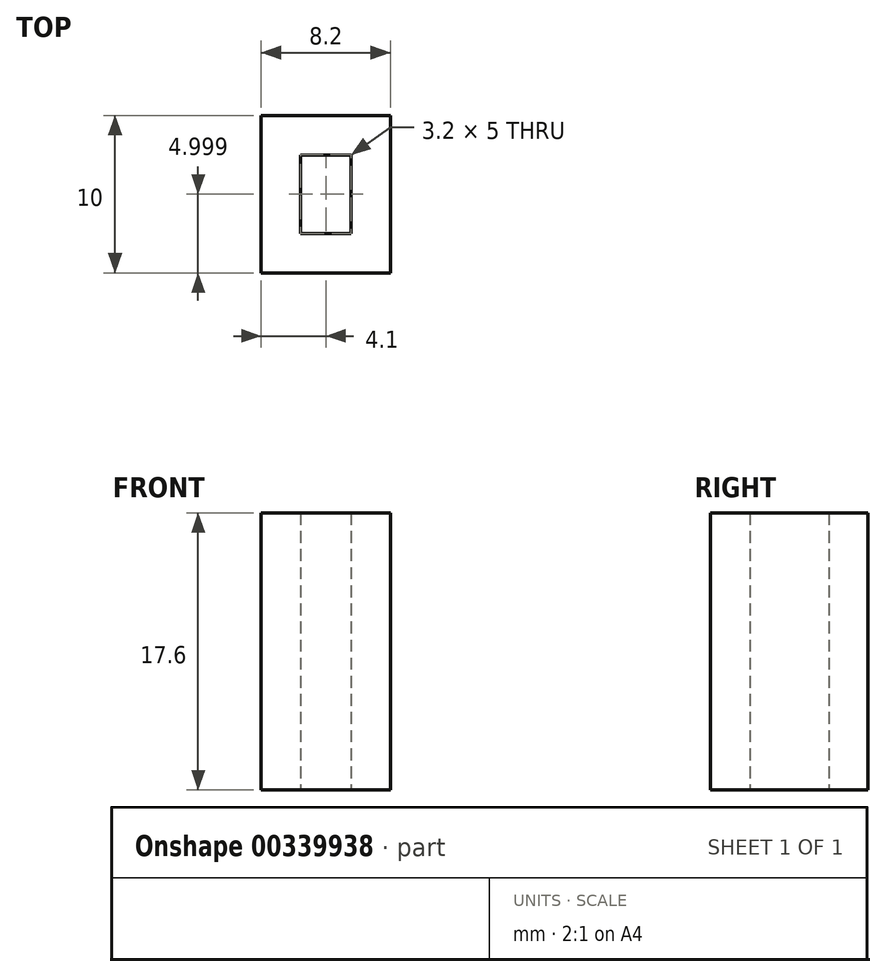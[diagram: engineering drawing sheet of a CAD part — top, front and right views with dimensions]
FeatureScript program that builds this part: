
annotation { "Feature Type Name" : "Feature", "Feature Type Description" : "" }
export const myFeature = defineFeature(function(context is Context, id is Id, definition is map)
    precondition{}
    {
        {
            var Q0;
            Q0=qCreatedBy(makeId("Top.planeOp"),FACE);
            var sketch = newSketch(context, id + "F0", { "sketchPlane" : qUnion([Q0])});
            skLineSegment(sketch, "E0.bottom", {"start": v(-14.33, 3.3) * mm, "end": v(-17.53, 3.3) * mm});
            skLineSegment(sketch, "E0.top", {"start": v(-14.33, -1.7) * mm, "end": v(-17.53, -1.7) * mm});
            skLineSegment(sketch, "E0.left", {"start": v(-14.33, 3.3) * mm, "end": v(-14.33, -1.7) * mm});
            skLineSegment(sketch, "E0.right", {"start": v(-17.53, 3.3) * mm, "end": v(-17.53, -1.7) * mm});
            skLineSegment(sketch, "E1", {"start": v(-20.03, -4.2) * mm, "end": v(-20.03, 5.8) * mm});
            skLineSegment(sketch, "E2", {"start": v(-11.83, -4.2) * mm, "end": v(-11.83, 5.8) * mm});
            skLineSegment(sketch, "E3", {"start": v(-11.83, -4.2) * mm, "end": v(-20.03, -4.2) * mm});
            skLineSegment(sketch, "E4", {"start": v(-20.03, 5.8) * mm, "end": v(-11.83, 5.8) * mm});
            skSolve(sketch);
        }
        {
            var Q0;
            Q0=makeQuery(id+"F0.imprint","IMPRINT",FACE,{"disambiguationData":[TD([[makeQuery(id+"F0.imprint","IMPRINT",EDGE,{"derivedFrom":sQuery(id+"F0.wireOp",EDGE,"Wre5aGVc-rJaU-OQyi-cZ9e-oLaSJC0nTDAK.bottom")}),-1.0]])]});
            var Q1;
            Q1=makeQuery(id+"F0.imprint","IMPRINT",FACE,{"disambiguationData":[TD([[makeQuery(id+"F0.imprint","IMPRINT",EDGE,{"derivedFrom":sQuery(id+"F0.wireOp",EDGE,"E0.bottom")}),-1.0]])]});
            extrude(context, id + "F1", {"entities" : qUnion([Q0, Q1]), "depth" : 17.6 * mm});
        }
    });
